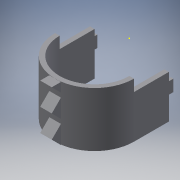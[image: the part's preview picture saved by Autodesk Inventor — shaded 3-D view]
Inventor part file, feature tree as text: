
AUTODESK INVENTOR PART (.ipt)
format: ipt  version: 2016 (Build 200138000, 138)  size: 218,624 bytes
history: native  units: in
note: dims shown in document units (in); Inventor stores cm internally (conversion verified against a paired STEP export)
features: sketch x9, extrude x8, reference x6, plane x1
ambient origin geometry x8: Origin, YZ Plane, XZ Plane, XY Plane, X Axis, Y Axis, Z Axis, Center Point
bodies: Solid1 (feature_tree)
feature tree (24):
  extrude  "Extrusion1"  Depth=1.5in TaperAngle=0.0deg
  extrude  "Extrusion2"  Depth=0.1969in TaperAngle=0.0deg
  extrude  "Extrusion3"  [1 undecoded]
  extrude  "Extrusion4"  Depth=0.3937in
  plane  "Work Plane1"
  sketch  "Sketch5"  dims[d12=1.9685in d14=0.9774in d15=0.3937in d17=1.0in d19=0.5in d20=0.0in]
  extrude  "Extrusion5"  Depth=0.5in TaperAngle=0.0deg
  extrude  "Extrusion6"  Depth=0.197in TaperAngle=0.0deg
  extrude  "Extrusion7"  Depth=0.5in TaperAngle=0.0deg
  extrude  "Extrusion8"  [1 undecoded]
  sketch  "Sketch1"  dims[d0=0.1969in d1=1.5in d2=0.0in]
  reference  "Reference1"
  sketch  "Sketch2"  dims[d3=4.6969in d4=0.0in d5=0.1969in d6=0.0in]
  sketch  "Sketch3"  dims[d7=0.1969in d8=0.0in d9=-1.697in]
  sketch  "Sketch4"  dims[d10=0.7874in d11=0.3937in]
  reference  "Reference2"
  sketch  "Sketch6"  dims[d21=0.197in d22=0.0in d23=100.0in d24=0.0in]
  sketch  "Sketch8"  dims[d25=0.5in d26=77.0in d27=0.0in]
  reference  "Reference3"
  reference  "Reference4"
  reference  "Reference5"
  reference  "Reference6"
  sketch  "Sketch9"
  sketch  "Sketch10"
note: 2 required parameter values undecoded (feature->parameter linkage not recoverable at this tier; creation-order binding heuristic only, values carry confidence <= 0.55)
